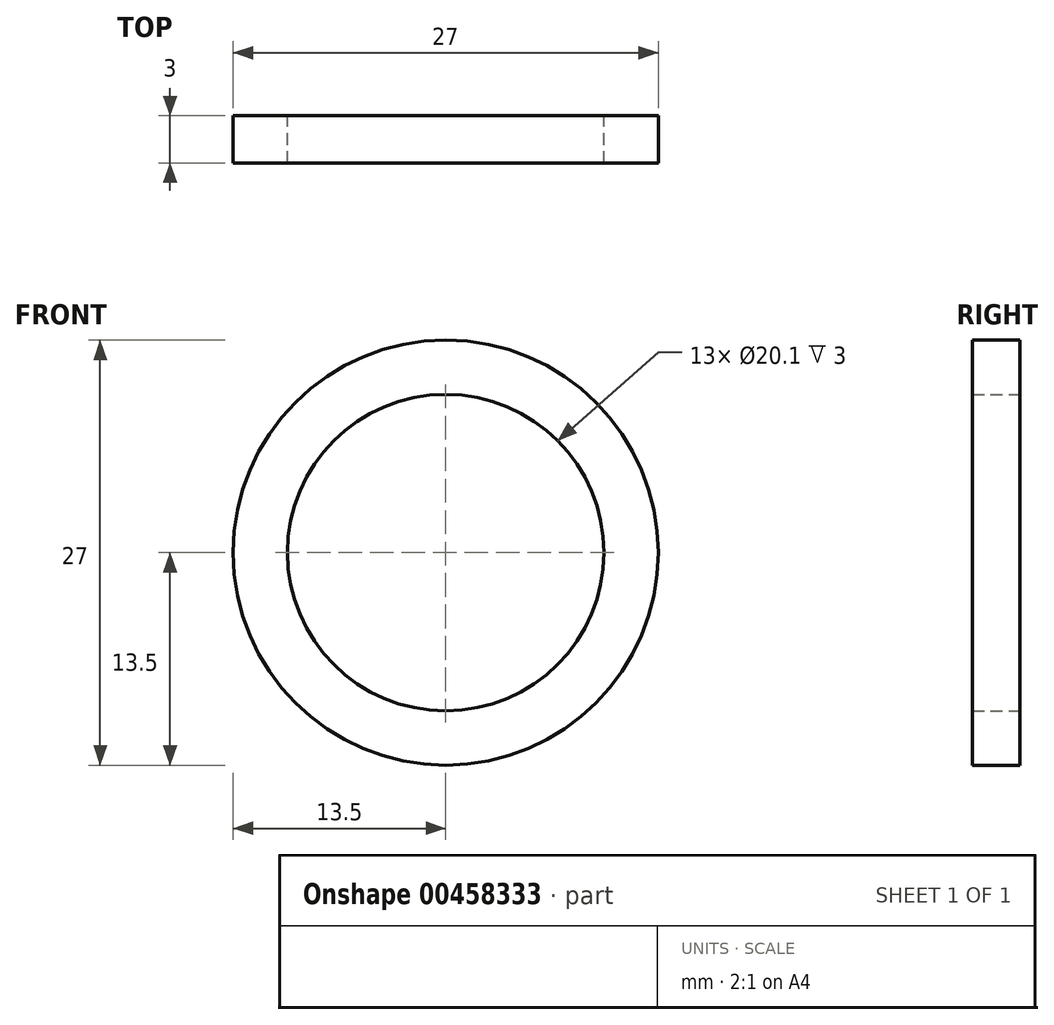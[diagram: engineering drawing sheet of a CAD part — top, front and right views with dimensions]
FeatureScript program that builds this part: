
annotation { "Feature Type Name" : "Feature", "Feature Type Description" : "" }
export const myFeature = defineFeature(function(context is Context, id is Id, definition is map)
    precondition{}
    {
        {
            var Q0;
            Q0=qCreatedBy(makeId("Front.planeOp"),FACE);
            var sketch = newSketch(context, id + "F0", { "sketchPlane" : qUnion([Q0])});
            skCircle(sketch, "E0", {"center": v(0, 0) * mm, "radius": 13.5 * mm});
            skCircle(sketch, "E1", {"center": v(0, 0) * mm, "radius": 10.05 * mm});
            skSolve(sketch);
        }
        {
            var Q0;
            Q0=makeQuery(id+"F0.imprint","IMPRINT",FACE,{"disambiguationData":[TD([[makeQuery(id+"F0.imprint","IMPRINT",EDGE,{"derivedFrom":sQuery(id+"F0.wireOp",EDGE,"E0")}),1.0]])]});
            extrude(context, id + "F1", {"entities" : qUnion([Q0]), "depth" : 3 * mm, "symmetric" : true});
        }
    });
